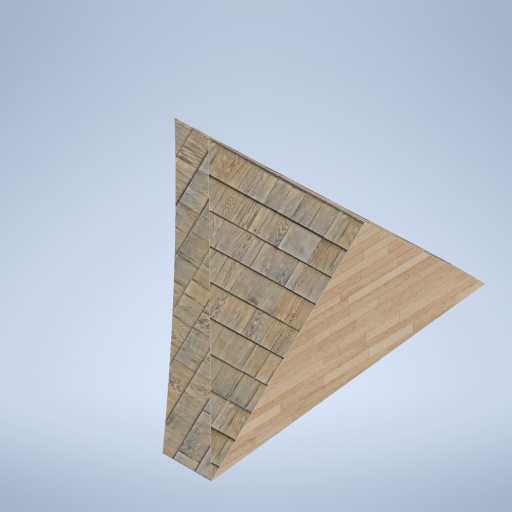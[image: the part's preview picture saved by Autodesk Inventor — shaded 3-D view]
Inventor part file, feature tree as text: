
AUTODESK INVENTOR PART (.ipt)
format: ipt  version: 2024.2 (Build 282272000, 272)  size: 471,040 bytes
history: native  units: in
note: dims shown in document units (in); Inventor stores cm internally (conversion verified against a paired STEP export)
features: sketch x7, plane x6, other x3
ambient origin geometry x8: Origin, YZ Plane, XZ Plane, XY Plane, X Axis, Y Axis, Z Axis, Center Point
bodies: Solid1 (feature_tree)
feature tree (16):
  other  "panel_pad_02 _MIR.ipt"
  other  "Solid1::panel_pad_02 _MIR.ipt"
  other  "TaggingFeature1"
  sketch  "Sketch1"  dims[d0=0.3937in]
  sketch  "Sketch2"
  sketch  "Sketch3"
  sketch  "Sketch6"
  sketch  "Sketch7"
  sketch  "Sketch8"
  sketch  "Sketch9"
  plane  "Work Plane1"
  plane  "Work Plane2"
  plane  "Work Plane3"
  plane  "Work Plane4"
  plane  "Work Plane5"
  plane  "Work Plane6"
